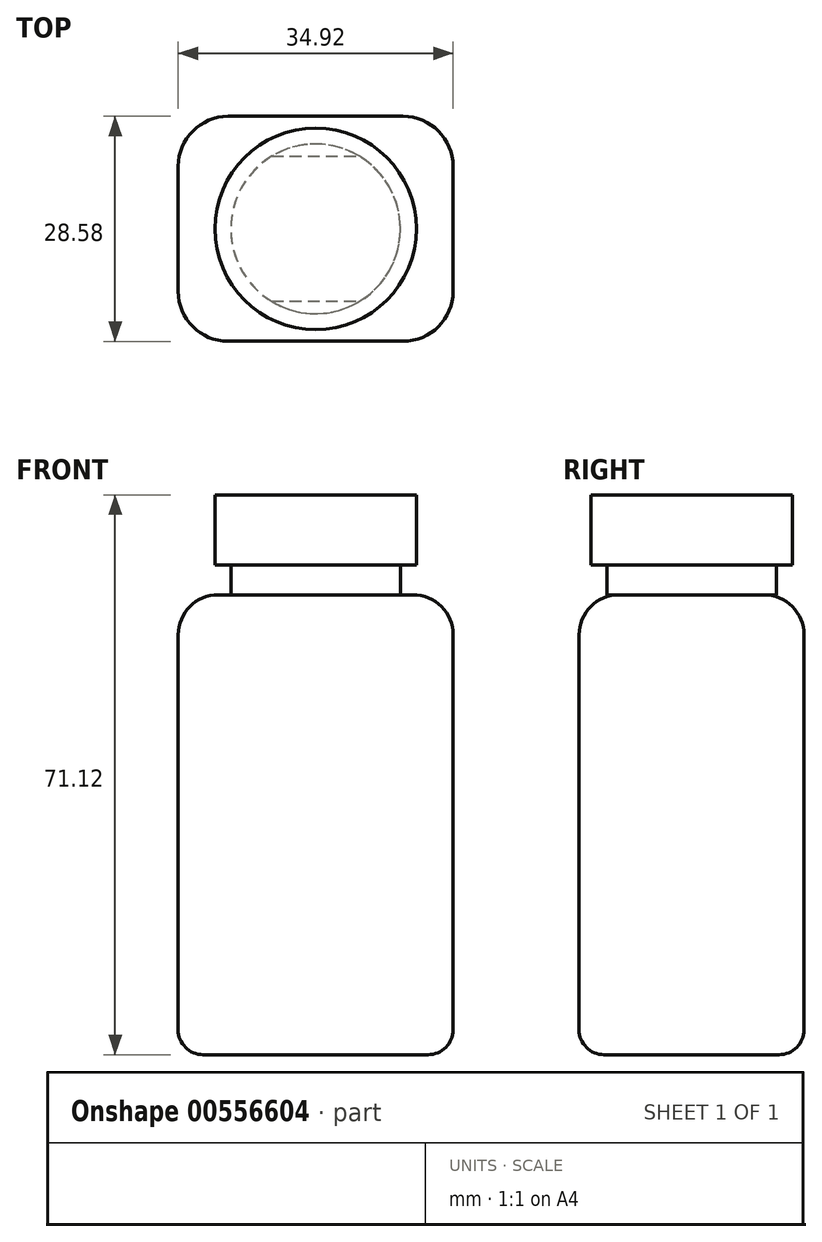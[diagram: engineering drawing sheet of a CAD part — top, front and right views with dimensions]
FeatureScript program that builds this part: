
annotation { "Feature Type Name" : "Feature", "Feature Type Description" : "" }
export const myFeature = defineFeature(function(context is Context, id is Id, definition is map)
    precondition{}
    {
        {
            var Q0;
            Q0=qCreatedBy(makeId("Top.planeOp"),FACE);
            var sketch = newSketch(context, id + "F0", { "sketchPlane" : qUnion([Q0])});
            skLineSegment(sketch, "E0.bottom", {"start": v(-11.11, -14.29) * mm, "end": v(11.11, -14.29) * mm});
            skLineSegment(sketch, "E0.top", {"start": v(-11.11, 14.29) * mm, "end": v(11.11, 14.29) * mm});
            skLineSegment(sketch, "E0.left", {"start": v(-17.46, -7.94) * mm, "end": v(-17.46, 7.94) * mm});
            skLineSegment(sketch, "E0.right", {"start": v(17.46, -7.94) * mm, "end": v(17.46, 7.94) * mm});
            skPoint(sketch, "E0.middle", {"position": v(0, 0) * mm});
            skPoint(sketch, "E1.visualSharp", {"position": v(-17.46, 14.29) * mm});
            skArc(sketch, "E1.filletArc", {"start": v(-11.11, 14.29) * mm, "mid": v(-15.6, 12.43) * mm, "end": v(-17.46, 7.94) * mm});
            skPoint(sketch, "E2.visualSharp", {"position": v(17.46, 14.29) * mm});
            skArc(sketch, "E2.filletArc", {"start": v(17.46, 7.94) * mm, "mid": v(15.6, 12.43) * mm, "end": v(11.11, 14.29) * mm});
            skPoint(sketch, "E3.visualSharp", {"position": v(17.46, -14.29) * mm});
            skArc(sketch, "E3.filletArc", {"start": v(11.11, -14.29) * mm, "mid": v(15.6, -12.43) * mm, "end": v(17.46, -7.94) * mm});
            skPoint(sketch, "E4.visualSharp", {"position": v(-17.46, -14.29) * mm});
            skArc(sketch, "E4.filletArc", {"start": v(-17.46, -7.94) * mm, "mid": v(-15.6, -12.43) * mm, "end": v(-11.11, -14.29) * mm});
            skSolve(sketch);
        }
        {
            var Q0;
            Q0 = qSketchRegion(id + "F0", true);
            extrude(context, id + "F1", {"entities" : qUnion([Q0]), "depth" : 55.63 * mm, "offsetDistance" : 25.4 * mm});
        }
        {
            var Q0;
            Q0=makeQuery(id+"F1.opExtrude","CAP_EDGE",EDGE,{"disambiguationData":[OSD([sQuery(id+"F0.wireOp",EDGE,"E3.filletArc")])],"isStart":false});
            fillet(context, id + "F2", {"entities" : qUnion([Q0]), "radius" : 5.08 * mm, "tangentPropagation" : true, "allowEdgeOverflow" : false});
        }
        {
            var Q0;
            Q0 = qSketchRegion(id + "F0", true);
            extrude(context, id + "F3", {"entities" : qUnion([Q0]), "operationType" : NewBodyOperationType.ADD, "oppositeDirection" : true, "depth" : 2.8 * mm, "offsetDistance" : 25.4 * mm});
        }
        {
            var Q0;
            Q0=makeQuery(id+"F3.opExtrude","CAP_EDGE",EDGE,{"disambiguationData":[OSD([sQuery(id+"F0.wireOp",EDGE,"E4.filletArc")])],"isStart":false});
            fillet(context, id + "F4", {"entities" : qUnion([Q0]), "radius" : 3.17 * mm, "tangentPropagation" : true, "allowEdgeOverflow" : false});
        }
        {
            var Q0;
            Q0=makeQuery(id+"F1.opExtrude","CAP_FACE",FACE,{"disambiguationData":[OSD([sQuery(id+"F0.wireOp",EDGE,"E0.bottom"),sQuery(id+"F0.wireOp",EDGE,"E0.top"),sQuery(id+"F0.wireOp",EDGE,"E0.left"),sQuery(id+"F0.wireOp",EDGE,"E0.right"),sQuery(id+"F0.wireOp",EDGE,"E1.filletArc"),sQuery(id+"F0.wireOp",EDGE,"E2.filletArc"),sQuery(id+"F0.wireOp",EDGE,"E3.filletArc"),sQuery(id+"F0.wireOp",EDGE,"E4.filletArc")])],"isStart":false});
            var sketch = newSketch(context, id + "F5", { "sketchPlane" : qUnion([Q0])});
            skCircle(sketch, "E5", {"center": v(0, 0) * mm, "radius": 10.77 * mm});
            skSolve(sketch);
        }
        {
            var Q0;
            Q0 = qSketchRegion(id + "F5", true);
            extrude(context, id + "F6", {"entities" : qUnion([Q0]), "operationType" : NewBodyOperationType.ADD, "depth" : 3.8 * mm, "offsetDistance" : 25.4 * mm});
        }
        {
            var Q0;
            Q0=makeQuery(id+"F6.opExtrude","CAP_FACE",FACE,{"disambiguationData":[OSD([sQuery(id+"F5.wireOp",EDGE,"E5")])],"isStart":false});
            var sketch = newSketch(context, id + "F7", { "sketchPlane" : qUnion([Q0])});
            skCircle(sketch, "E6", {"center": v(0, 0) * mm, "radius": 12.8 * mm});
            skSolve(sketch);
        }
        {
            var Q0;
            Q0 = qSketchRegion(id + "F7", true);
            extrude(context, id + "F8", {"entities" : qUnion([Q0]), "operationType" : NewBodyOperationType.ADD, "depth" : 8.9 * mm, "offsetDistance" : 25.4 * mm});
        }
    });
